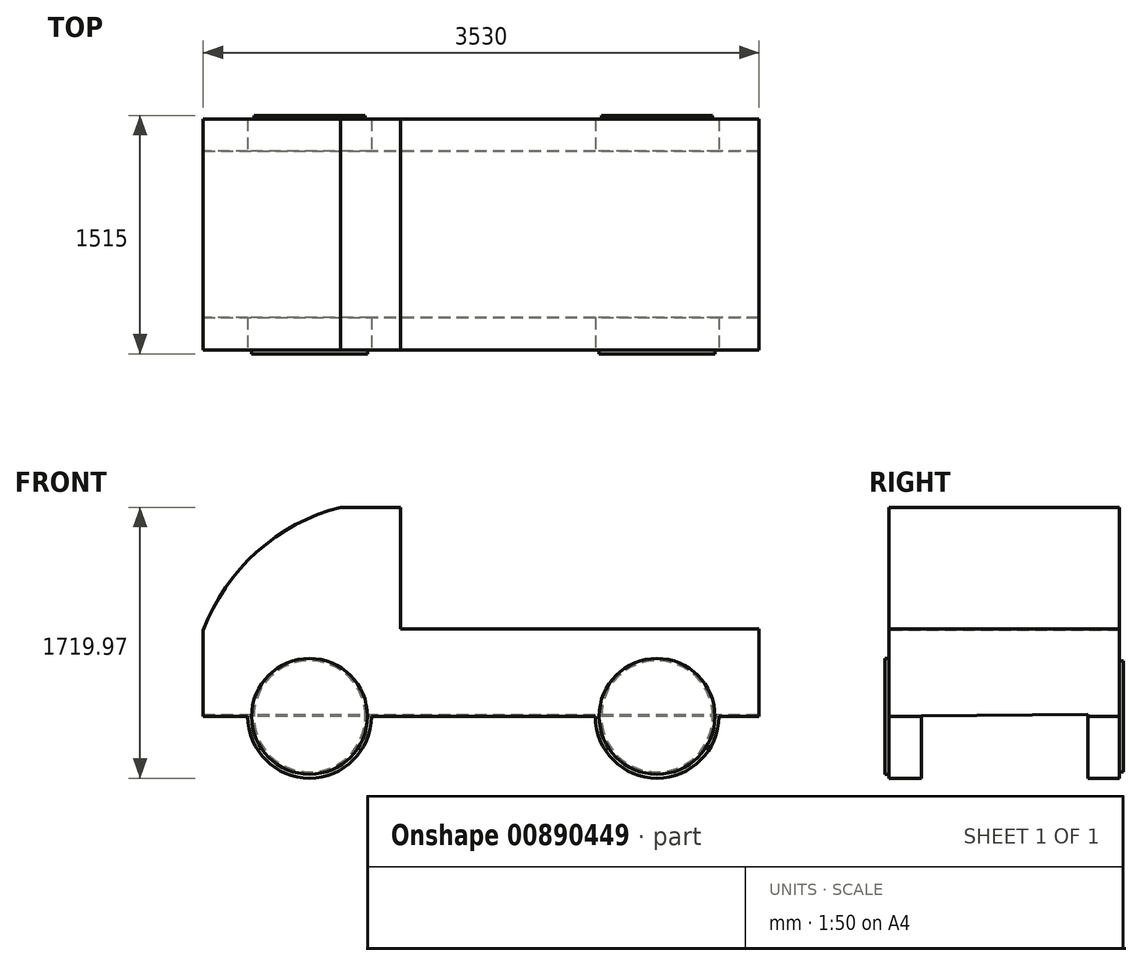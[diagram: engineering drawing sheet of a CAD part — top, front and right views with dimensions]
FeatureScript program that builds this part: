
annotation { "Feature Type Name" : "Feature", "Feature Type Description" : "" }
export const myFeature = defineFeature(function(context is Context, id is Id, definition is map)
    precondition{}
    {
        {
            var Q0;
            Q0=qCreatedBy(makeId("Top.planeOp"),FACE);
            var sketch = newSketch(context, id + "F0", { "sketchPlane" : qUnion([Q0])});
            skLineSegment(sketch, "E0.bottom", {"start": v(0, -4.01) * mm, "end": v(-3530, -4.01) * mm});
            skLineSegment(sketch, "E0.top", {"start": v(0, 1460.99) * mm, "end": v(-3530, 1460.99) * mm});
            skLineSegment(sketch, "E0.left", {"start": v(0, -4.01) * mm, "end": v(0, 1460.99) * mm});
            skLineSegment(sketch, "E0.right", {"start": v(-3530, -4.01) * mm, "end": v(-3530, 1460.99) * mm});
            skSolve(sketch);
        }
        {
            var Q0;
            Q0=makeQuery(id+"F0.imprint","IMPRINT",FACE,{"disambiguationData":[TD([[makeQuery(id+"F0.imprint","IMPRINT",EDGE,{"derivedFrom":sQuery(id+"F0.wireOp",EDGE,"E0.bottom")}),-1.0]])]});
            extrude(context, id + "F1", {"entities" : qUnion([Q0]), "depth" : 1720 * mm, "offsetDistance" : 25 * mm});
        }
        {
            var Q0;
            Q0=makeQuery(id+"F1.opExtrude","SWEPT_FACE",FACE,{"disambiguationData":[OSD([sQuery(id+"F0.wireOp",EDGE,"E0.bottom")])]});
            var sketch = newSketch(context, id + "F2", { "sketchPlane" : qUnion([Q0])});
            skLineSegment(sketch, "E1", {"start": v(-3530, 0) * mm, "end": v(-3530, 392.33) * mm});
            skLineSegment(sketch, "E2", {"start": v(-3530, 392.33) * mm, "end": v(0, 392.33) * mm});
            skLineSegment(sketch, "E3", {"start": v(0, 392.33) * mm, "end": v(0, 0) * mm});
            skArc(sketch, "E4", {"start": v(-2656.38, 1720) * mm, "mid": v(-3189.73, 1436.73) * mm, "end": v(-3530, 937.8) * mm});
            skLineSegment(sketch, "E5", {"start": v(-2656.38, 1720) * mm, "end": v(-2276.16, 1720) * mm});
            skLineSegment(sketch, "E6", {"start": v(-2276.16, 1720) * mm, "end": v(-2276.16, 947.91) * mm});
            skLineSegment(sketch, "E7", {"start": v(-2276.16, 947.91) * mm, "end": v(0, 947.91) * mm});
            skLineSegment(sketch, "E8", {"start": v(0, 947.91) * mm, "end": v(0, 392.33) * mm});
            skCircle(sketch, "E9", {"center": v(-2854.45, 392.33) * mm, "radius": 392.3 * mm});
            skCircle(sketch, "E10", {"center": v(-647.55, 392.33) * mm, "radius": 392.3 * mm});
            skSolve(sketch);
        }
        {
            var Q0;
            Q0=makeQuery(id+"F1.opExtrude","SWEPT_FACE",FACE,{"disambiguationData":[OSD([sQuery(id+"F0.wireOp",EDGE,"E0.left")])]});
            var sketch = newSketch(context, id + "F3", { "sketchPlane" : qUnion([Q0])});
            skLineSegment(sketch, "E11", {"start": v(0, 0) * mm, "end": v(-4.01, 392.28) * mm});
            skLineSegment(sketch, "E12", {"start": v(-4.01, 392.28) * mm, "end": v(1460.99, 407.27) * mm});
            skLineSegment(sketch, "E13", {"start": v(1460.99, 407.27) * mm, "end": v(1460.99, 0) * mm});
            skLineSegment(sketch, "E14", {"start": v(1460.99, 0) * mm, "end": v(1259.78, 0) * mm});
            skLineSegment(sketch, "E15", {"start": v(1259.78, 0) * mm, "end": v(1259.78, 405.21) * mm});
            skLineSegment(sketch, "E16", {"start": v(0, 0) * mm, "end": v(201.2, 0) * mm});
            skLineSegment(sketch, "E17", {"start": v(201.2, 0) * mm, "end": v(201.2, 394.38) * mm});
            skSolve(sketch);
        }
        {
            var Q0;
            {var subQ0=sQuery(id+"F3.wireOp",EDGE,"E15");Q0=makeQuery(id+"F3.imprint","IMPRINT",FACE,{"disambiguationData":[TD([[makeQuery(id+"F3.imprint","IMPRINT",EDGE,{"derivedFrom":subQ0}),1.0]])]});}
            extrude(context, id + "F4", {"entities" : qUnion([Q0]), "operationType" : NewBodyOperationType.REMOVE, "oppositeDirection" : true, "depth" : 3600 * mm, "offsetDistance" : 25 * mm});
        }
        {
            var Q0;
            {var subQ5=sQuery(id+"F2.wireOp",EDGE,"E1");Q0=makeQuery(id+"F2.imprint","IMPRINT",FACE,{"disambiguationData":[TD([[makeQuery(id+"F2.imprint","IMPRINT",EDGE,{"derivedFrom":subQ5}),1.0]])]});}
            var Q1;
            {var subQ0=sQuery(id+"F2.wireOp",EDGE,"E6");Q1=makeQuery(id+"F2.imprint","IMPRINT",FACE,{"disambiguationData":[TD([[makeQuery(id+"F2.imprint","IMPRINT",EDGE,{"derivedFrom":subQ0}),1.0]])]});}
            var Q2;
            {var subQ0=sQuery(id+"F2.wireOp",EDGE,"E4");Q2=makeQuery(id+"F2.imprint","IMPRINT",FACE,{"disambiguationData":[TD([[makeQuery(id+"F2.imprint","IMPRINT",EDGE,{"derivedFrom":subQ0}),-1.0]])]});}
            extrude(context, id + "F5", {"entities" : qUnion([Q0, Q1, Q2]), "operationType" : NewBodyOperationType.REMOVE, "oppositeDirection" : true, "depth" : 2000 * mm, "offsetDistance" : 25 * mm});
        }
        {
            var Q0;
            Q0=makeQuery(id+"F1.opExtrude","SWEPT_FACE",FACE,{"disambiguationData":[OSD([sQuery(id+"F0.wireOp",EDGE,"E0.bottom")])]});
            var sketch = newSketch(context, id + "F6", { "sketchPlane" : qUnion([Q0])});
            skLineSegment(sketch, "E18", {"start": v(-3246.75, 392.33) * mm, "end": v(-2462.15, 392.33) * mm});
            skLineSegment(sketch, "E19", {"start": v(-2462.15, 392.33) * mm, "end": v(-1039.85, 392.33) * mm});
            skLineSegment(sketch, "E20", {"start": v(-1039.85, 392.33) * mm, "end": v(-255.25, 392.33) * mm});
            skCircle(sketch, "E21", {"center": v(-2854.45, 392.33) * mm, "radius": 367.87 * mm});
            skCircle(sketch, "E22", {"center": v(-647.55, 392.33) * mm, "radius": 367.85 * mm});
            skSolve(sketch);
        }
        {
            var Q0;
            {var subQ0=sQuery(id+"F6.wireOp",EDGE,"E21");var subQ1=sQuery(id+"F6.wireOp",EDGE,"E18");var subQ2=makeQuery(id+"F6.imprint","INTERSECT",VERTEX,{"disambiguationData":[OD(0.0)],"derivedFrom":[subQ1,subQ0]});Q0=makeQuery(id+"F6.imprint","IMPRINT",FACE,{"disambiguationData":[TD([[makeQuery(id+"F6.imprint","IMPRINT",EDGE,{"disambiguationData":[TD([[subQ2,-1.0]])],"derivedFrom":subQ1}),1.0]])]});}
            var Q1;
            {var subQ0=sQuery(id+"F6.wireOp",EDGE,"E21");var subQ1=sQuery(id+"F6.wireOp",EDGE,"E18");var subQ2=makeQuery(id+"F6.imprint","INTERSECT",VERTEX,{"disambiguationData":[OD(0.0)],"derivedFrom":[subQ1,subQ0]});Q1=makeQuery(id+"F6.imprint","IMPRINT",FACE,{"disambiguationData":[TD([[makeQuery(id+"F6.imprint","IMPRINT",EDGE,{"disambiguationData":[TD([[subQ2,-1.0]])],"derivedFrom":subQ1}),-1.0]])]});}
            var Q2;
            {var subQ0=sQuery(id+"F6.wireOp",EDGE,"E22");var subQ1=sQuery(id+"F6.wireOp",EDGE,"E20");var subQ2=makeQuery(id+"F6.imprint","INTERSECT",VERTEX,{"disambiguationData":[OD(0.0)],"derivedFrom":[subQ1,subQ0]});Q2=makeQuery(id+"F6.imprint","IMPRINT",FACE,{"disambiguationData":[TD([[makeQuery(id+"F6.imprint","IMPRINT",EDGE,{"disambiguationData":[TD([[subQ2,-1.0]])],"derivedFrom":subQ1}),1.0]])]});}
            var Q3;
            {var subQ0=sQuery(id+"F6.wireOp",EDGE,"E22");var subQ1=sQuery(id+"F6.wireOp",EDGE,"E20");var subQ2=makeQuery(id+"F6.imprint","INTERSECT",VERTEX,{"disambiguationData":[OD(0.0)],"derivedFrom":[subQ1,subQ0]});Q3=makeQuery(id+"F6.imprint","IMPRINT",FACE,{"disambiguationData":[TD([[makeQuery(id+"F6.imprint","IMPRINT",EDGE,{"disambiguationData":[TD([[subQ2,-1.0]])],"derivedFrom":subQ1}),-1.0]])]});}
            extrude(context, id + "F7", {"entities" : qUnion([Q0, Q1, Q2, Q3]), "depth" : 25 * mm, "offsetDistance" : 25 * mm});
        }
        {
            var Q0;
            Q0=makeQuery(id+"F1.opExtrude","SWEPT_FACE",FACE,{"disambiguationData":[OSD([sQuery(id+"F0.wireOp",EDGE,"E0.top")])]});
            var sketch = newSketch(context, id + "F8", { "sketchPlane" : qUnion([Q0])});
            skLineSegment(sketch, "E23", {"start": v(255.25, 392.33) * mm, "end": v(1039.85, 392.33) * mm});
            skLineSegment(sketch, "E24", {"start": v(1039.85, 392.33) * mm, "end": v(2462.15, 392.33) * mm});
            skLineSegment(sketch, "E25", {"start": v(2462.15, 392.33) * mm, "end": v(3246.75, 392.33) * mm});
            skCircle(sketch, "E26", {"center": v(647.55, 392.33) * mm, "radius": 352.85 * mm});
            skCircle(sketch, "E27", {"center": v(2854.45, 392.33) * mm, "radius": 352.85 * mm});
            skSolve(sketch);
        }
        {
            var Q0;
            {var subQ0=sQuery(id+"F8.wireOp",EDGE,"E26");var subQ1=sQuery(id+"F8.wireOp",EDGE,"E23");var subQ2=makeQuery(id+"F8.imprint","INTERSECT",VERTEX,{"disambiguationData":[OD(0.0)],"derivedFrom":[subQ1,subQ0]});Q0=makeQuery(id+"F8.imprint","IMPRINT",FACE,{"disambiguationData":[TD([[makeQuery(id+"F8.imprint","IMPRINT",EDGE,{"disambiguationData":[TD([[subQ2,-1.0]])],"derivedFrom":subQ1}),1.0]])]});}
            var Q1;
            {var subQ0=sQuery(id+"F8.wireOp",EDGE,"E26");var subQ1=sQuery(id+"F8.wireOp",EDGE,"E23");var subQ2=makeQuery(id+"F8.imprint","INTERSECT",VERTEX,{"disambiguationData":[OD(0.0)],"derivedFrom":[subQ1,subQ0]});Q1=makeQuery(id+"F8.imprint","IMPRINT",FACE,{"disambiguationData":[TD([[makeQuery(id+"F8.imprint","IMPRINT",EDGE,{"disambiguationData":[TD([[subQ2,-1.0]])],"derivedFrom":subQ1}),-1.0]])]});}
            var Q2;
            {var subQ0=sQuery(id+"F8.wireOp",EDGE,"E27");var subQ1=sQuery(id+"F8.wireOp",EDGE,"E25");var subQ2=makeQuery(id+"F8.imprint","INTERSECT",VERTEX,{"disambiguationData":[OD(0.0)],"derivedFrom":[subQ1,subQ0]});Q2=makeQuery(id+"F8.imprint","IMPRINT",FACE,{"disambiguationData":[TD([[makeQuery(id+"F8.imprint","IMPRINT",EDGE,{"disambiguationData":[TD([[subQ2,-1.0]])],"derivedFrom":subQ1}),1.0]])]});}
            var Q3;
            {var subQ0=sQuery(id+"F8.wireOp",EDGE,"E27");var subQ1=sQuery(id+"F8.wireOp",EDGE,"E25");var subQ2=makeQuery(id+"F8.imprint","INTERSECT",VERTEX,{"disambiguationData":[OD(0.0)],"derivedFrom":[subQ1,subQ0]});Q3=makeQuery(id+"F8.imprint","IMPRINT",FACE,{"disambiguationData":[TD([[makeQuery(id+"F8.imprint","IMPRINT",EDGE,{"disambiguationData":[TD([[subQ2,-1.0]])],"derivedFrom":subQ1}),-1.0]])]});}
            extrude(context, id + "F9", {"entities" : qUnion([Q0, Q1, Q2, Q3]), "depth" : 25 * mm, "offsetDistance" : 25 * mm});
        }
    });
